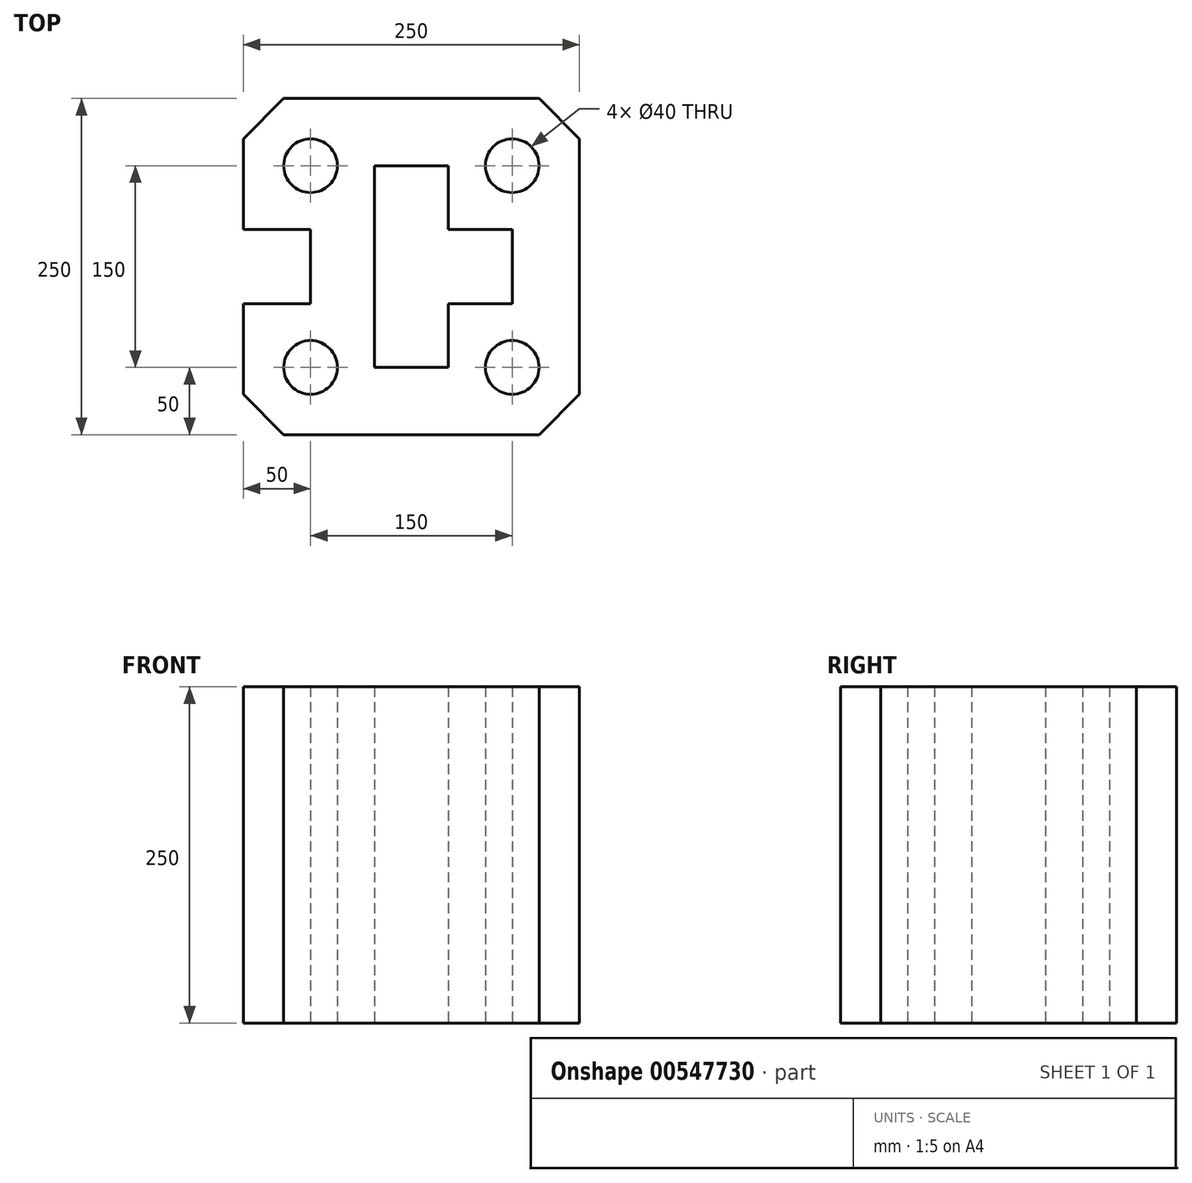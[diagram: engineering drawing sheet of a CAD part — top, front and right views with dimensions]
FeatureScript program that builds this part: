
annotation { "Feature Type Name" : "Feature", "Feature Type Description" : "" }
export const myFeature = defineFeature(function(context is Context, id is Id, definition is map)
    precondition{}
    {
        {
            var Q0;
            Q0=qCreatedBy(makeId("Top.planeOp"),FACE);
            var sketch = newSketch(context, id + "F0", { "sketchPlane" : qUnion([Q0])});
            skLineSegment(sketch, "E0", {"start": v(0, 0) * mm, "end": v(-200, 0) * mm, "construction": true});
            skLineSegment(sketch, "E1", {"start": v(0, 0) * mm, "end": v(0, 184.9) * mm, "construction": true});
            skLineSegment(sketch, "E2.bottom", {"start": v(95, 125) * mm, "end": v(-95, 125) * mm});
            skLineSegment(sketch, "E2.top", {"start": v(95, -125) * mm, "end": v(-95, -125) * mm});
            skLineSegment(sketch, "E2.left", {"start": v(125, 95) * mm, "end": v(125, -95) * mm});
            skLineSegment(sketch, "E2.right", {"start": v(-125, 95) * mm, "end": v(-125, 27.5) * mm});
            skLineSegment(sketch, "E3.bottom", {"start": v(-125, 27.5) * mm, "end": v(-75, 27.5) * mm});
            skLineSegment(sketch, "E3.top", {"start": v(-125, -27.5) * mm, "end": v(-75, -27.5) * mm});
            skLineSegment(sketch, "E3.right", {"start": v(-75, 27.5) * mm, "end": v(-75, -27.5) * mm});
            skPoint(sketch, "E3.middle", {"position": v(-100, 0) * mm});
            skLineSegment(sketch, "E4.trimOffspring", {"start": v(-125, -27.5) * mm, "end": v(-125, -95) * mm});
            skLineSegment(sketch, "E5", {"start": v(-95, 125) * mm, "end": v(-125, 95) * mm});
            skLineSegment(sketch, "E6", {"start": v(-95, -125) * mm, "end": v(-125, -95) * mm});
            skLineSegment(sketch, "E7", {"start": v(125, -95) * mm, "end": v(95, -125) * mm});
            skLineSegment(sketch, "E8", {"start": v(95, 125) * mm, "end": v(125, 95) * mm});
            skPoint(sketch, "E9.orphan", {"position": v(-125, 125) * mm});
            skPoint(sketch, "E10.orphan", {"position": v(125, 125) * mm});
            skPoint(sketch, "E11.orphan", {"position": v(125, -125) * mm});
            skPoint(sketch, "E12.orphan", {"position": v(-125, -125) * mm});
            skLineSegment(sketch, "E13", {"start": v(-27.5, 75) * mm, "end": v(-27.5, -75) * mm});
            skLineSegment(sketch, "E14", {"start": v(-27.5, -75) * mm, "end": v(27.5, -75) * mm});
            skLineSegment(sketch, "E15", {"start": v(27.5, -75) * mm, "end": v(27.5, -27.5) * mm});
            skLineSegment(sketch, "E16", {"start": v(27.5, -27.5) * mm, "end": v(75, -27.5) * mm});
            skLineSegment(sketch, "E17", {"start": v(75, -27.5) * mm, "end": v(75, 27.5) * mm});
            skLineSegment(sketch, "E18", {"start": v(75, 27.5) * mm, "end": v(27.5, 27.5) * mm});
            skLineSegment(sketch, "E19", {"start": v(27.5, 27.5) * mm, "end": v(27.5, 75) * mm});
            skLineSegment(sketch, "E20", {"start": v(27.5, 75) * mm, "end": v(-27.5, 75) * mm});
            skCircle(sketch, "E21", {"center": v(-75, 75) * mm, "radius": 20 * mm});
            skCircle(sketch, "E22", {"center": v(-75, -75) * mm, "radius": 20 * mm});
            skCircle(sketch, "E23", {"center": v(75, -75) * mm, "radius": 20 * mm});
            skCircle(sketch, "E24", {"center": v(75, 75) * mm, "radius": 20 * mm});
            skSolve(sketch);
        }
        {
            var Q0;
            Q0=qSketchRegion(id+"F0",true);
            extrude(context, id + "F1", {"entities" : qUnion([Q0]), "endBound" : BoundingType.SYMMETRIC, "depth" : 250 * mm, "offsetDistance" : 25 * mm});
        }
    });
